# Revit family: ERA_Вентилятор крышный_ERF
name_source: partatom
category: Оборудование
units: mm (PartAtom-declared; Revit-internal decimal feet)

## family parameters
Всегда вертикально = Да
Классификация = Нет
На основе рабочей плоскости = Нет
Общий = Нет
При загрузке вырезать с полостями = Нет
Размер круглого соединителя = Использовать диаметр
Тип детали = Вставляется
Точка расчета площади = Нет

## types (6) — shared parameters
ADSK_URL документации изделия = https://era.trade
ADSK_URL страницы изделия = https://era.trade
ADSK_Версия Revit = 2019
ADSK_Версия семейства = Ver.1 2025-02
ADSK_Единица измерения = шт.
ADSK_Завод-изготовитель = ООО «ЭРА»
ADSK_Классификация нагрузок = Электродвигатель вентилятора
ADSK_Количество = 1
ADSK_Количество фаз = 1
ADSK_Количество фаз числовое = 1
ADSK_Коэффициент мощности = 0.8
ADSK_Материал = ERA_Пластик_Серый
ADSK_Напряжение = 230 В
D1 = 9 мм
ERA_IP вентилятора = X4
ERA_IP двигателя = 44
ERA_Гарантия = 2 года
ERA_Количество в транспортной упаковке = 1
ERA_Контакты = 8 (4912) 70-16-76, 8 (4912) 24-16-00
ERA_Материал корпуса = Оцинкованная сталь
ERA_Материал лопастей = Композитный пластик
ERA_Принцип вентиляции = Вытяжной
ERA_Рабочий механизм = Центробежный
ERA_Размещение = Крышное
ERA_Страна производитель = Россия
ERA_Температурный диапазон работы = от минус 30°С до плюс 60 °С
ERA_Торговая марка = ERA PRO
ERA_Управление = Механическое
ERA_Цвет = Серый
H1 = 15 мм
LT = ERA_Вентилятор крышный_ERF
URL = https://era.trade
Изготовитель = ООО «ЭРА»
Производитель_Контакты_Телефон = 8 (4912) 70-16-76, 8 (4912) 24-16-00

## per-type parameters (varying)
| type | ADSK_Масса | ADSK_Масса_Текст | ADSK_Наименование | ADSK_Номинальная мощность | ADSK_Полная мощность | ADSK_Размер_Высота | ADSK_Размер_Длина | ADSK_Размер_Ширина | ADSK_Ток | Code1 | ERA_Уровень шума | ERA_Частота вращения | H2 | H3 | L | Vis_1 | Vis_2 | Vis_2_3 | Vis_3 | Vis_4 | Vis_5 | Vis_6 |
| ERF 192 | 4.4 | 4.4 | Вентилятор крышный ERF 192 | 70 Вт | 70 В·А | 179 мм | 370 мм | 370 мм | 0 А | 1 | 62 | 2650 | 84 мм | 80 мм | 300 мм | Да | Нет | Нет | Нет | Нет | Нет | Нет |
| ERF 220 | 5.1 | 5.1 | Вентилятор крышный ERF 220 | 115 Вт | 115 В·А | 190 мм | 370 мм | 370 мм | 1 А | 2 | 67 | 2350 | 80 мм | 95 мм | 300 мм | Нет | Да | Да | Нет | Нет | Нет | Нет |
| ERF 225 | 5.9 | 5.9 | Вентилятор крышный ERF 225 | 150 Вт | 150 В·А | 209 мм | 370 мм | 370 мм | 1 А | 3 | 70 | 2500 | 99 мм | 95 мм | 300 мм | Нет | Нет | Да | Да | Нет | Нет | Нет |
| ERF 250 | 6.6 | 6.6 | Вентилятор крышный ERF 250 | 210 Вт | 210 В·А | 220 мм | 370 мм | 370 мм | 1 А | 4 | 72 | 2500 | 110 мм | 95 мм | 300 мм | Нет | Нет | Нет | Нет | Да | Нет | Нет |
| ERF 280 | 7.9 | 7.9 | Вентилятор крышный ERF 280 | 280 Вт | 280 В·А | 220 мм | 450 мм | 450 мм | 1 А | 5 | 74 | 2450 | 110 мм | 95 мм | 370 мм | Нет | Нет | Нет | Нет | Нет | Да | Нет |
| ERF 310 | 8.8 | 8.8 | Вентилятор крышный ERF 310 | 160 Вт | 160 В·А | 280 мм | 450 мм | 450 мм | 1 А | 6 | 63 | 1600 | 167 мм | 98 мм | 370 мм | Нет | Нет | Нет | Нет | Нет | Нет | Да |

note: column(s) folded — value = type name in every type: ADSK_Код изделия, ADSK_Марка, ADSK_Обозначение
